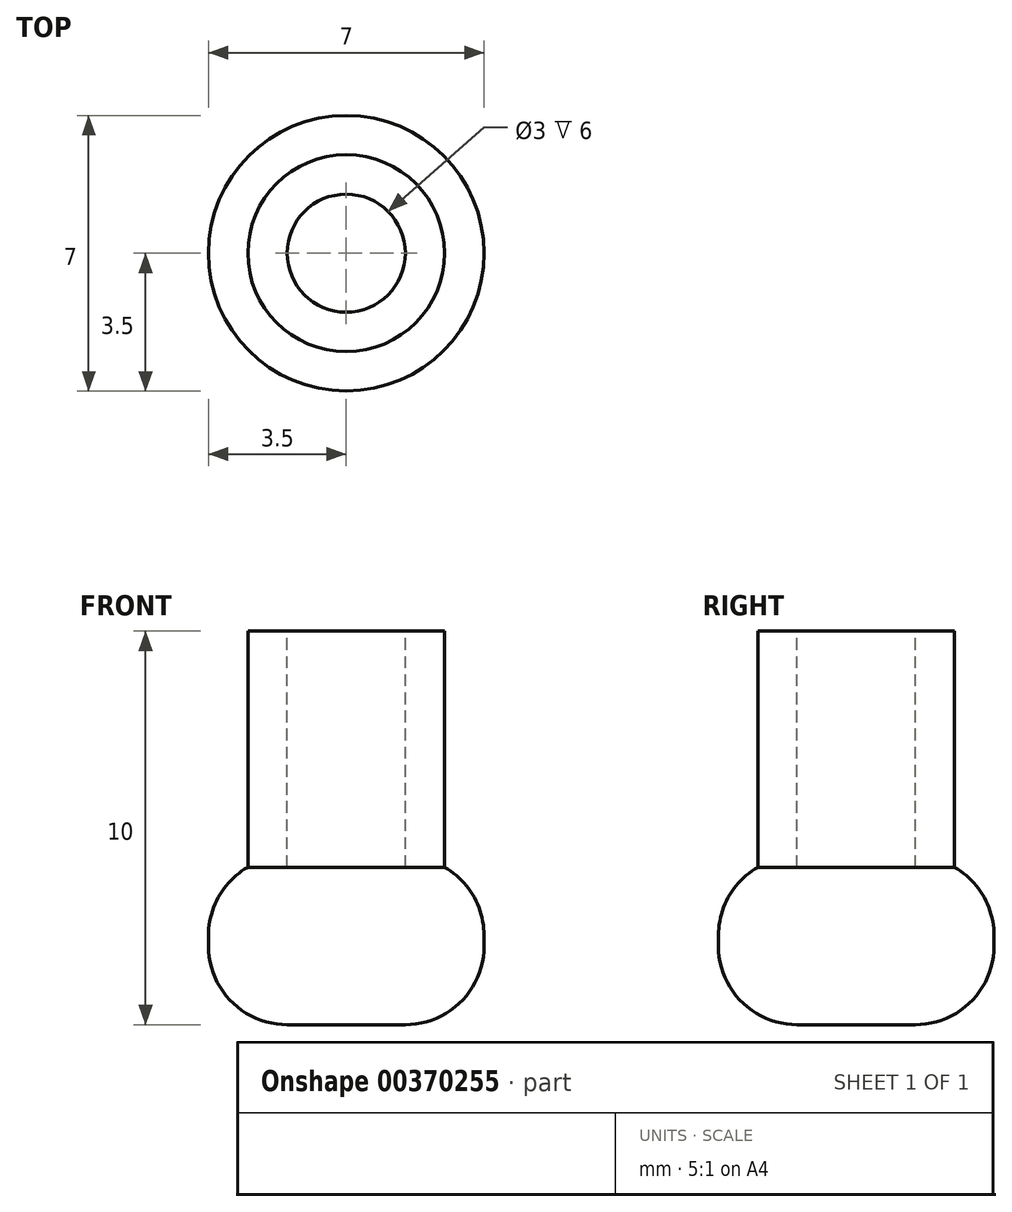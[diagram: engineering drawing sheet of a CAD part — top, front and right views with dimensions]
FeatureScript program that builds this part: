
annotation { "Feature Type Name" : "Feature", "Feature Type Description" : "" }
export const myFeature = defineFeature(function(context is Context, id is Id, definition is map)
    precondition{}
    {
        {
            var Q0;
            Q0=qCreatedBy(makeId("Top.planeOp"),FACE);
            var sketch = newSketch(context, id + "F0", { "sketchPlane" : qUnion([Q0])});
            skCircle(sketch, "E0", {"center": v(0, 0) * mm, "radius": 1.5 * mm});
            skCircle(sketch, "E1", {"center": v(0, 0) * mm, "radius": 2.5 * mm});
            skSolve(sketch);
        }
        {
            var Q0;
            Q0=makeQuery(id+"F0.imprint","IMPRINT",FACE,{"disambiguationData":[TD([[makeQuery(id+"F0.imprint","IMPRINT",EDGE,{"derivedFrom":sQuery(id+"F0.wireOp",EDGE,"E0")}),-1.0]])]});
            extrude(context, id + "F1", {"entities" : qUnion([Q0]), "oppositeDirection" : true, "depth" : 6 * mm, "offsetDistance" : 25 * mm});
        }
        {
            var Q0;
            Q0=makeQuery(id+"F0.imprint","IMPRINT",FACE,{"disambiguationData":[TD([[makeQuery(id+"F0.imprint","IMPRINT",EDGE,{"derivedFrom":sQuery(id+"F0.wireOp",EDGE,"E0")}),1.0]])]});
            extrude(context, id + "F2", {"entities" : qUnion([Q0]), "operationType" : NewBodyOperationType.REMOVE, "oppositeDirection" : true, "depth" : 7 * mm, "offsetDistance" : 25 * mm});
        }
        {
            var Q0;
            Q0=makeQuery(id+"F1.opExtrude","CAP_FACE",FACE,{"disambiguationData":[OSD([sQuery(id+"F0.wireOp",EDGE,"E0"),sQuery(id+"F0.wireOp",EDGE,"E1")])],"isStart":false});
            var sketch = newSketch(context, id + "F3", { "sketchPlane" : qUnion([Q0])});
            skCircle(sketch, "E2", {"center": v(0, 0) * mm, "radius": 3.5 * mm});
            skSolve(sketch);
        }
        {
            var Q0;
            Q0=makeQuery(id+"F3.imprint","IMPRINT",FACE,{"disambiguationData":[TD([[makeQuery(id+"F3.imprint","IMPRINT",EDGE,{"derivedFrom":sQuery(id+"F3.wireOp",EDGE,"E2")}),1.0]])]});
            var Q1;
            Q1=makeQuery(id+"F3.imprint","IMPRINT",FACE,{"disambiguationData":[TD([[makeQuery(id+"F3.imprint","IMPRINT",EDGE,{"derivedFrom":makeQuery(id+"F1.opExtrude","CAP_EDGE",EDGE,{"disambiguationData":[OSD([sQuery(id+"F0.wireOp",EDGE,"E0")])],"isStart":false})}),1.0]])]});
            var Q2;
            Q2=makeQuery(id+"F3.imprint","IMPRINT",FACE,{"disambiguationData":[TD([[makeQuery(id+"F3.imprint","IMPRINT",EDGE,{"derivedFrom":makeQuery(id+"F1.opExtrude","CAP_EDGE",EDGE,{"disambiguationData":[OSD([sQuery(id+"F0.wireOp",EDGE,"E0")])],"isStart":false})}),-1.0]])]});
            extrude(context, id + "F4", {"entities" : qUnion([Q0, Q1, Q2]), "operationType" : NewBodyOperationType.ADD, "depth" : 4 * mm, "offsetDistance" : 25 * mm});
        }
        {
            var Q0;
            Q0=makeQuery(id+"F4.opExtrude","CAP_EDGE",EDGE,{"disambiguationData":[OSD([sQuery(id+"F3.wireOp",EDGE,"E2")])],"isStart":false});
            var Q1;
            Q1=makeQuery(id+"F4.opExtrude","CAP_EDGE",EDGE,{"disambiguationData":[OSD([sQuery(id+"F3.wireOp",EDGE,"E2")])],"isStart":true});
            fillet(context, id + "F5", {"entities" : qUnion([Q0, Q1]), "tangentPropagation" : true, "radius" : 2 * mm, "defaultsChanged" : false, "vertexSettings" : [], "allowEdgeOverflow" : false});
        }
    });
